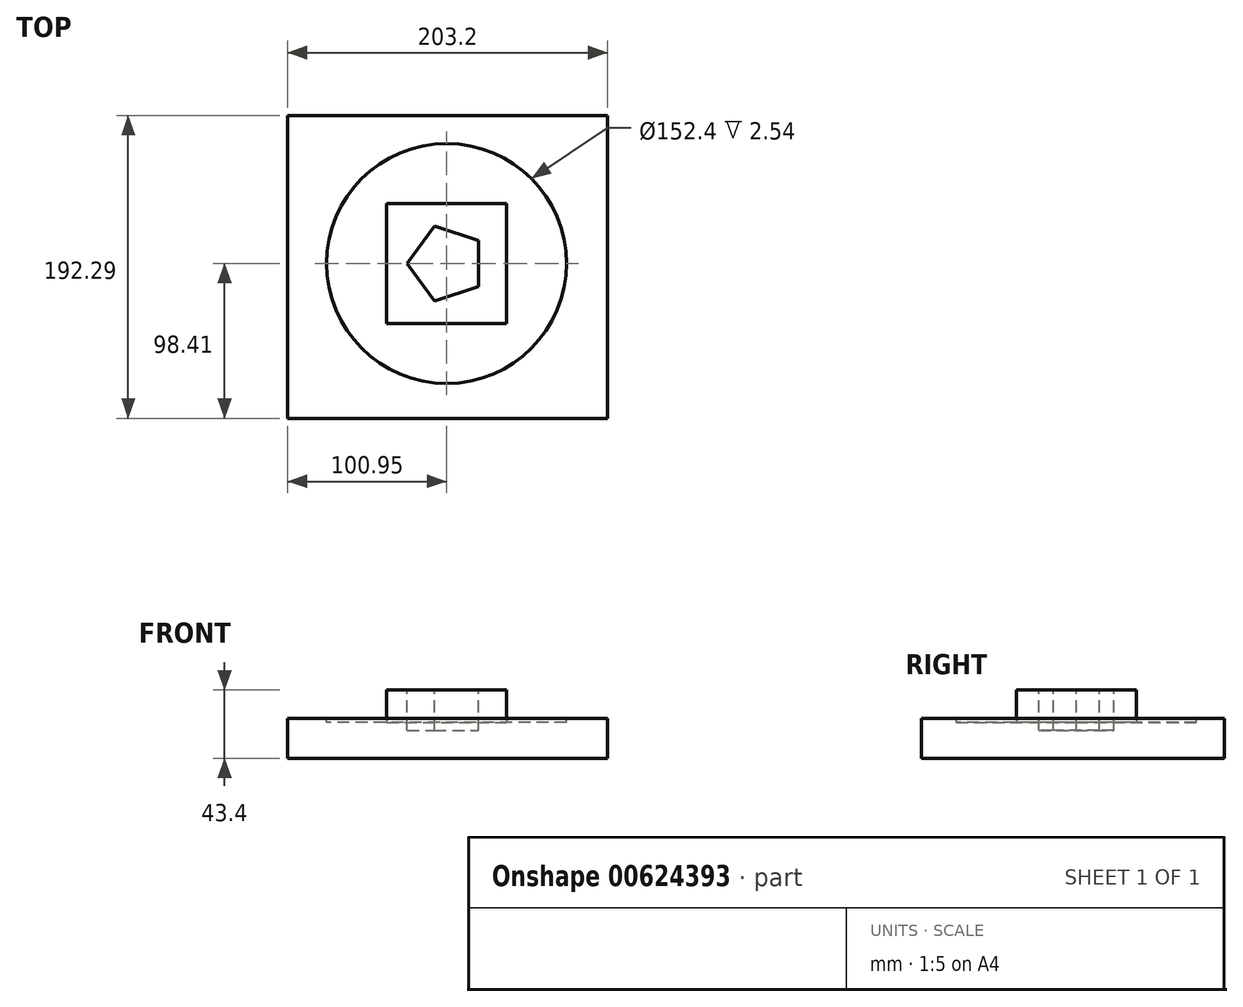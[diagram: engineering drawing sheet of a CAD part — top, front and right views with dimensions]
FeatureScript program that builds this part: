
annotation { "Feature Type Name" : "Feature", "Feature Type Description" : "" }
export const myFeature = defineFeature(function(context is Context, id is Id, definition is map)
    precondition{}
    {
        {
            var Q0;
            Q0=qCreatedBy(makeId("Top.planeOp"),FACE);
            var sketch = newSketch(context, id + "F0", { "sketchPlane" : qUnion([Q0])});
            skLineSegment(sketch, "E0.bottom", {"start": v(-100.95, 93.88) * mm, "end": v(102.25, 93.88) * mm});
            skLineSegment(sketch, "E0.top", {"start": v(-100.95, -98.4) * mm, "end": v(102.25, -98.4) * mm});
            skLineSegment(sketch, "E0.left", {"start": v(-100.95, 93.88) * mm, "end": v(-100.95, -98.4) * mm});
            skLineSegment(sketch, "E0.right", {"start": v(102.25, 93.88) * mm, "end": v(102.25, -98.4) * mm});
            skSolve(sketch);
        }
        {
            var Q0;
            Q0 = qSketchRegion(id + "F0", true);
            extrude(context, id + "F1", {"entities" : qUnion([Q0]), "depth" : 25.4 * mm, "offsetDistance" : 25.4 * mm});
        }
        {
            var Q0;
            Q0=makeQuery(id+"F1.opExtrude","CAP_FACE",FACE,{"disambiguationData":[OSD([sQuery(id+"F0.wireOp",EDGE,"E0.bottom"),sQuery(id+"F0.wireOp",EDGE,"E0.top"),sQuery(id+"F0.wireOp",EDGE,"E0.left"),sQuery(id+"F0.wireOp",EDGE,"E0.right")])],"isStart":false});
            var sketch = newSketch(context, id + "F2", { "sketchPlane" : qUnion([Q0])});
            skCircle(sketch, "E1", {"center": v(0, 0) * mm, "radius": 76.2 * mm});
            skSolve(sketch);
        }
        {
            var Q0;
            Q0 = qSketchRegion(id + "F2", true);
            extrude(context, id + "F3", {"entities" : qUnion([Q0]), "operationType" : NewBodyOperationType.REMOVE, "oppositeDirection" : true, "depth" : 2.54 * mm, "offsetDistance" : 25.4 * mm});
        }
        {
            var Q0;
            Q0=makeQuery(id+"F3.boolean.opBoolean","COPY",FACE,{"derivedFrom":makeQuery(id+"F3.opExtrude","CAP_FACE",FACE,{"disambiguationData":[OSD([sQuery(id+"F2.wireOp",EDGE,"E1")])],"isStart":false})});
            var sketch = newSketch(context, id + "F4", { "sketchPlane" : qUnion([Q0])});
            skLineSegment(sketch, "E2.bottom", {"start": v(-38.1, 38.1) * mm, "end": v(38.1, 38.1) * mm});
            skLineSegment(sketch, "E2.top", {"start": v(-38.1, -38.1) * mm, "end": v(38.1, -38.1) * mm});
            skLineSegment(sketch, "E2.left", {"start": v(-38.1, 38.1) * mm, "end": v(-38.1, -38.1) * mm});
            skLineSegment(sketch, "E2.right", {"start": v(38.1, 38.1) * mm, "end": v(38.1, -38.1) * mm});
            skPoint(sketch, "E2.middle", {"position": v(0, 0) * mm});
            skSolve(sketch);
        }
        {
            var Q0;
            Q0 = qSketchRegion(id + "F4", true);
            extrude(context, id + "F5", {"entities" : qUnion([Q0]), "operationType" : NewBodyOperationType.ADD, "depth" : 2.54 * mm, "offsetDistance" : 25.4 * mm});
        }
        {
            var Q0;
            Q0=makeQuery(id+"F5.opExtrude","CAP_FACE",FACE,{"disambiguationData":[OSD([sQuery(id+"F4.wireOp",EDGE,"E2.bottom"),sQuery(id+"F4.wireOp",EDGE,"E2.top"),sQuery(id+"F4.wireOp",EDGE,"E2.left"),sQuery(id+"F4.wireOp",EDGE,"E2.right")])],"isStart":false});
            var sketch = newSketch(context, id + "F6", { "sketchPlane" : qUnion([Q0])});
            skCircle(sketch, "E3.cCircle", {"center": v(0, 0) * mm, "radius": 20.2 * mm, "construction": true});
            skLineSegment(sketch, "E3.0", {"start": v(20.2, 14.68) * mm, "end": v(20.2, -14.68) * mm});
            skLineSegment(sketch, "E3.1", {"start": v(20.2, -14.68) * mm, "end": v(-7.72, -23.76) * mm});
            skLineSegment(sketch, "E3.2", {"start": v(-7.72, -23.76) * mm, "end": v(-24.98, 0) * mm});
            skLineSegment(sketch, "E3.3", {"start": v(-24.98, 0) * mm, "end": v(-7.72, 23.76) * mm});
            skLineSegment(sketch, "E3.4", {"start": v(-7.72, 23.76) * mm, "end": v(20.2, 14.68) * mm});
            skPoint(sketch, "E3.0.midPoint", {"position": v(20.2, 0) * mm});
            skSolve(sketch);
        }
        {
            var Q0;
            Q0 = qSketchRegion(id + "F6", true);
            extrude(context, id + "F7", {"entities" : qUnion([Q0]), "operationType" : NewBodyOperationType.REMOVE, "oppositeDirection" : true, "depth" : 7.62 * mm, "offsetDistance" : 25.4 * mm});
        }
        {
            var Q0;
            Q0=makeQuery(id+"F5.opExtrude","CAP_FACE",FACE,{"disambiguationData":[OSD([sQuery(id+"F4.wireOp",EDGE,"E2.bottom"),sQuery(id+"F4.wireOp",EDGE,"E2.top"),sQuery(id+"F4.wireOp",EDGE,"E2.left"),sQuery(id+"F4.wireOp",EDGE,"E2.right")])],"isStart":false});
            extrude(context, id + "F8", {"entities" : qUnion([Q0]), "operationType" : NewBodyOperationType.ADD, "depth" : 18 * mm, "offsetDistance" : 25 * mm});
        }
    });
